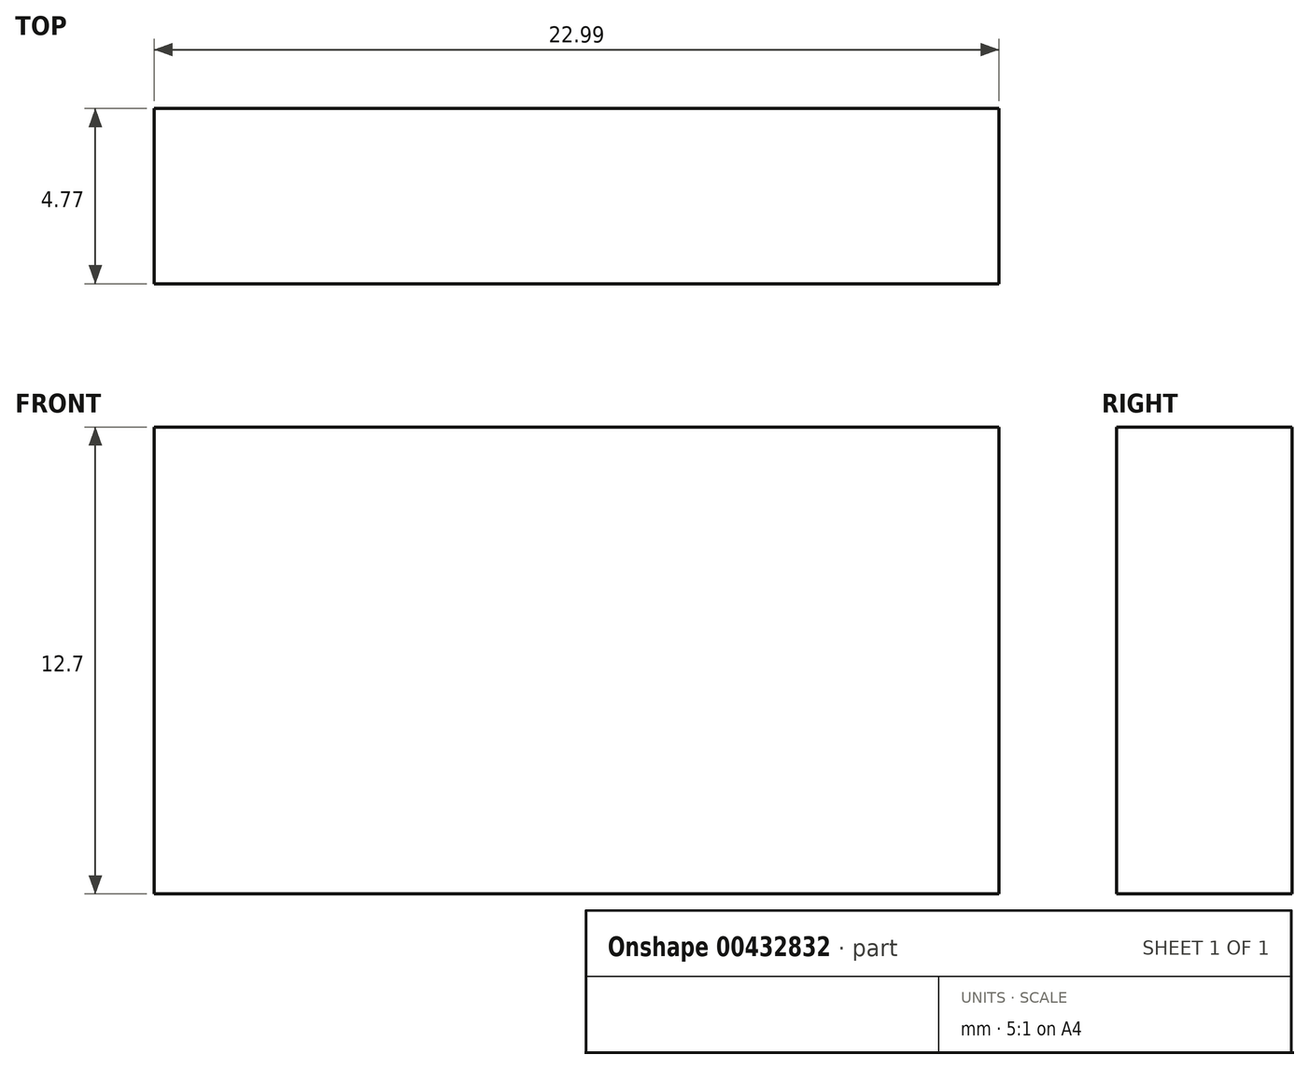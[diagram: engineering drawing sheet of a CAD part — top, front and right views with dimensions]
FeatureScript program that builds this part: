
annotation { "Feature Type Name" : "Feature", "Feature Type Description" : "" }
export const myFeature = defineFeature(function(context is Context, id is Id, definition is map)
    precondition{}
    {
        {
            var Q0;
            Q0=qCreatedBy(makeId("Top.planeOp"),FACE);
            var sketch = newSketch(context, id + "F0", { "sketchPlane" : qUnion([Q0])});
            skLineSegment(sketch, "E0.bottom", {"start": v(-4.38, 3.56) * mm, "end": v(18.6, 3.56) * mm});
            skLineSegment(sketch, "E0.top", {"start": v(-4.38, -1.21) * mm, "end": v(18.6, -1.21) * mm});
            skLineSegment(sketch, "E0.left", {"start": v(-4.38, 3.56) * mm, "end": v(-4.38, -1.21) * mm});
            skLineSegment(sketch, "E0.right", {"start": v(18.6, 3.56) * mm, "end": v(18.6, -1.21) * mm});
            skSolve(sketch);
        }
        {
            var Q0;
            Q0=makeQuery(id+"F0.imprint","IMPRINT",FACE,{"disambiguationData":[TD([[makeQuery(id+"F0.imprint","IMPRINT",EDGE,{"derivedFrom":sQuery(id+"F0.wireOp",EDGE,"E0.bottom")}),-1.0]])]});
            extrude(context, id + "F1", {"entities" : qUnion([Q0]), "depth" : 12.7 * mm});
        }
    });
